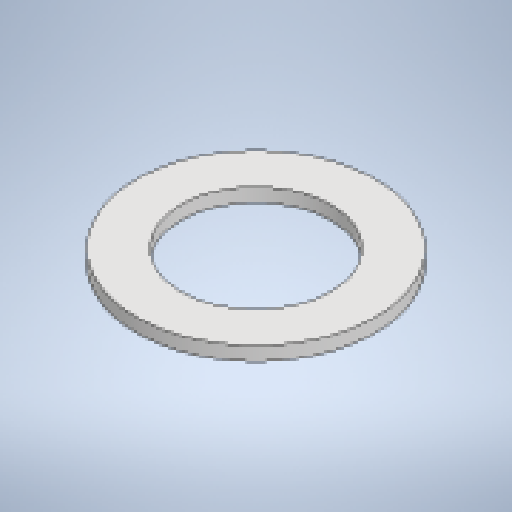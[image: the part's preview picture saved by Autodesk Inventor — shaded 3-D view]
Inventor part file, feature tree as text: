
AUTODESK INVENTOR PART (.ipt)
format: ipt  version: 2025 (Build 290162010, 162A)  size: 176,640 bytes
history: native  units: mm
features: other x2, sheet_metal_op x1, sketch x1
ambient origin geometry x8: Origin, YZ Plane, XZ Plane, XY Plane, X Axis, Y Axis, Z Axis, Center Point
bodies: Body1 (feature_tree)
feature tree (4):
  sheet_metal_op  "Face2"
  sketch  "Sketch2"  dims[d14=8.0mm d25=88.0mm d27=140.0mm]
  other  "Plate2"
  other  "Definition1"
